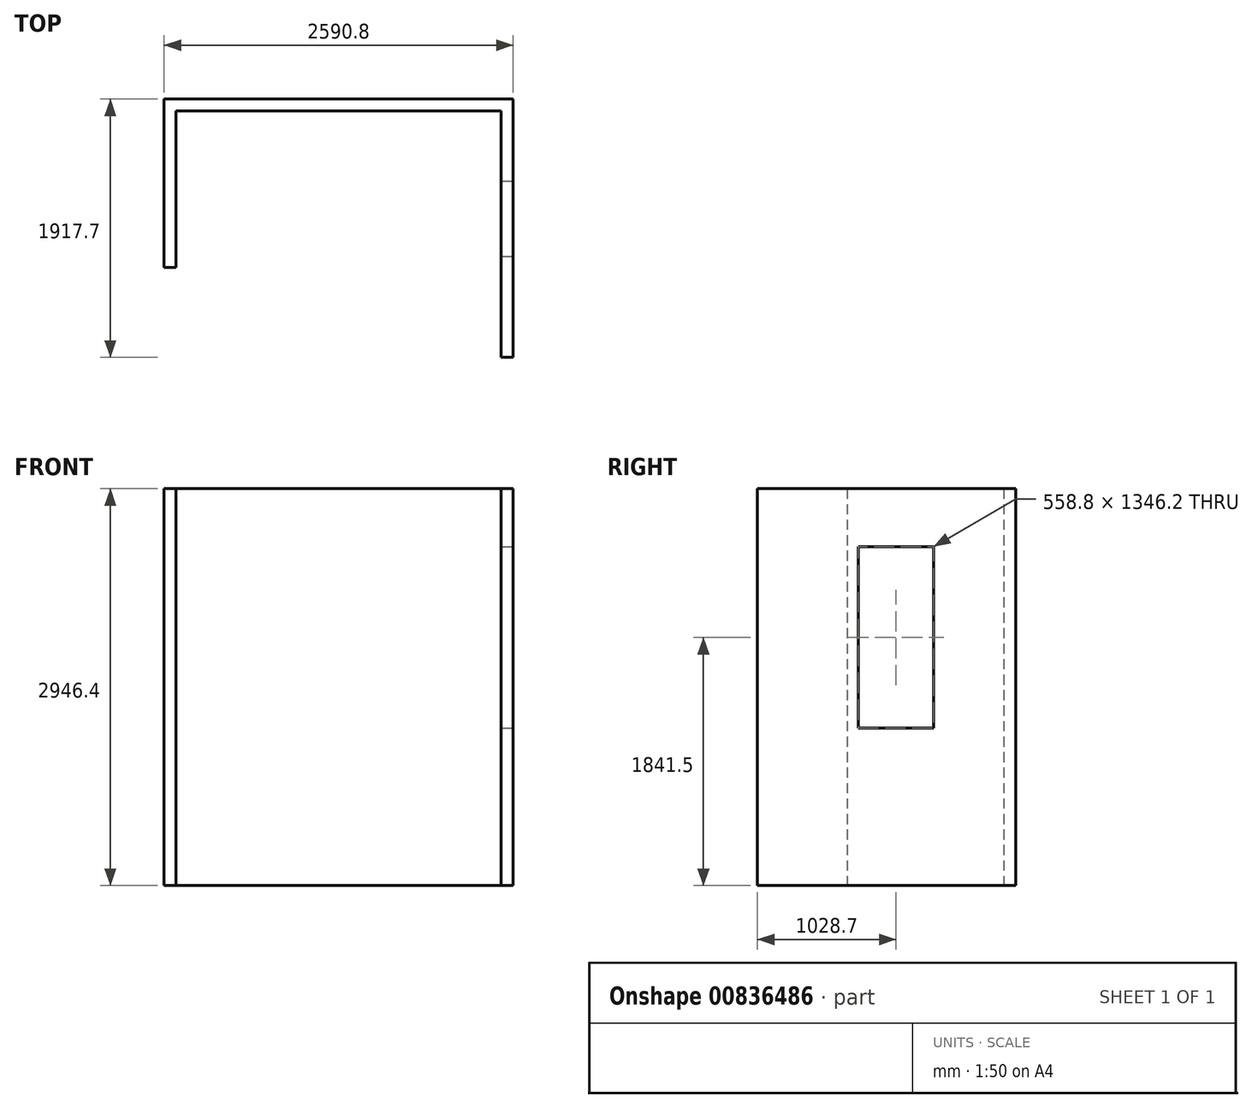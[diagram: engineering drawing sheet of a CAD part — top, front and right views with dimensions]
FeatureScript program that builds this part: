
annotation { "Feature Type Name" : "Feature", "Feature Type Description" : "" }
export const myFeature = defineFeature(function(context is Context, id is Id, definition is map)
    precondition{}
    {
        {
            var Q0;
            Q0=qCreatedBy(makeId("Top.planeOp"),FACE);
            var sketch = newSketch(context, id + "F0", { "sketchPlane" : qUnion([Q0])});
            skLineSegment(sketch, "E0", {"start": v(-1206.5, 0) * mm, "end": v(1206.5, 0) * mm});
            skLineSegment(sketch, "E1", {"start": v(1206.5, 0) * mm, "end": v(1206.5, -1828.8) * mm});
            skLineSegment(sketch, "E2", {"start": v(1206.5, -1828.8) * mm, "end": v(1295.4, -1828.8) * mm});
            skLineSegment(sketch, "E3", {"start": v(1295.4, -1828.8) * mm, "end": v(1295.4, 88.9) * mm});
            skLineSegment(sketch, "E4", {"start": v(1295.4, 88.9) * mm, "end": v(-1295.4, 88.9) * mm});
            skLineSegment(sketch, "E5", {"start": v(-1295.4, 88.9) * mm, "end": v(-1295.4, -1162.05) * mm});
            skLineSegment(sketch, "E6", {"start": v(-1295.4, -1162.05) * mm, "end": v(-1206.5, -1162.05) * mm});
            skLineSegment(sketch, "E7", {"start": v(-1206.5, -1162.05) * mm, "end": v(-1206.5, 0) * mm});
            skSolve(sketch);
        }
        {
            var Q0;
            Q0=qSketchRegion(id+"F0",true);
            extrude(context, id + "F1", {"entities" : qUnion([Q0]), "offsetDistance" : 25.4 * mm, "depth" : 2946.4 * mm});
        }
        {
            var Q0;
            Q0=makeQuery(id+"F1.opExtrude","SWEPT_FACE",FACE,{"disambiguationData":[OSD([sQuery(id+"F0.wireOp",EDGE,"E3")])]});
            var sketch = newSketch(context, id + "F2", { "sketchPlane" : qUnion([Q0])});
            skLineSegment(sketch, "E8.bottom", {"start": v(-1079.5, 2514.6) * mm, "end": v(-520.7, 2514.6) * mm});
            skLineSegment(sketch, "E8.top", {"start": v(-1079.5, 1168.4) * mm, "end": v(-520.7, 1168.4) * mm});
            skLineSegment(sketch, "E8.left", {"start": v(-1079.5, 2514.6) * mm, "end": v(-1079.5, 1168.4) * mm});
            skLineSegment(sketch, "E8.right", {"start": v(-520.7, 2514.6) * mm, "end": v(-520.7, 1168.4) * mm});
            skSolve(sketch);
        }
        {
            var Q0;
            Q0=makeQuery(id+"F2.imprint","IMPRINT",FACE,{"disambiguationData":[TD([[makeQuery(id+"F2.imprint","IMPRINT",EDGE,{"derivedFrom":sQuery(id+"F2.wireOp",EDGE,"E8.bottom")}),-1.0]])]});
            extrude(context, id + "F3", {"entities" : qUnion([Q0]), "operationType" : NewBodyOperationType.REMOVE, "endBound" : BoundingType.UP_TO_NEXT, "oppositeDirection" : true, "depth" : 25.4 * mm, "offsetDistance" : 25.4 * mm});
        }
    });
